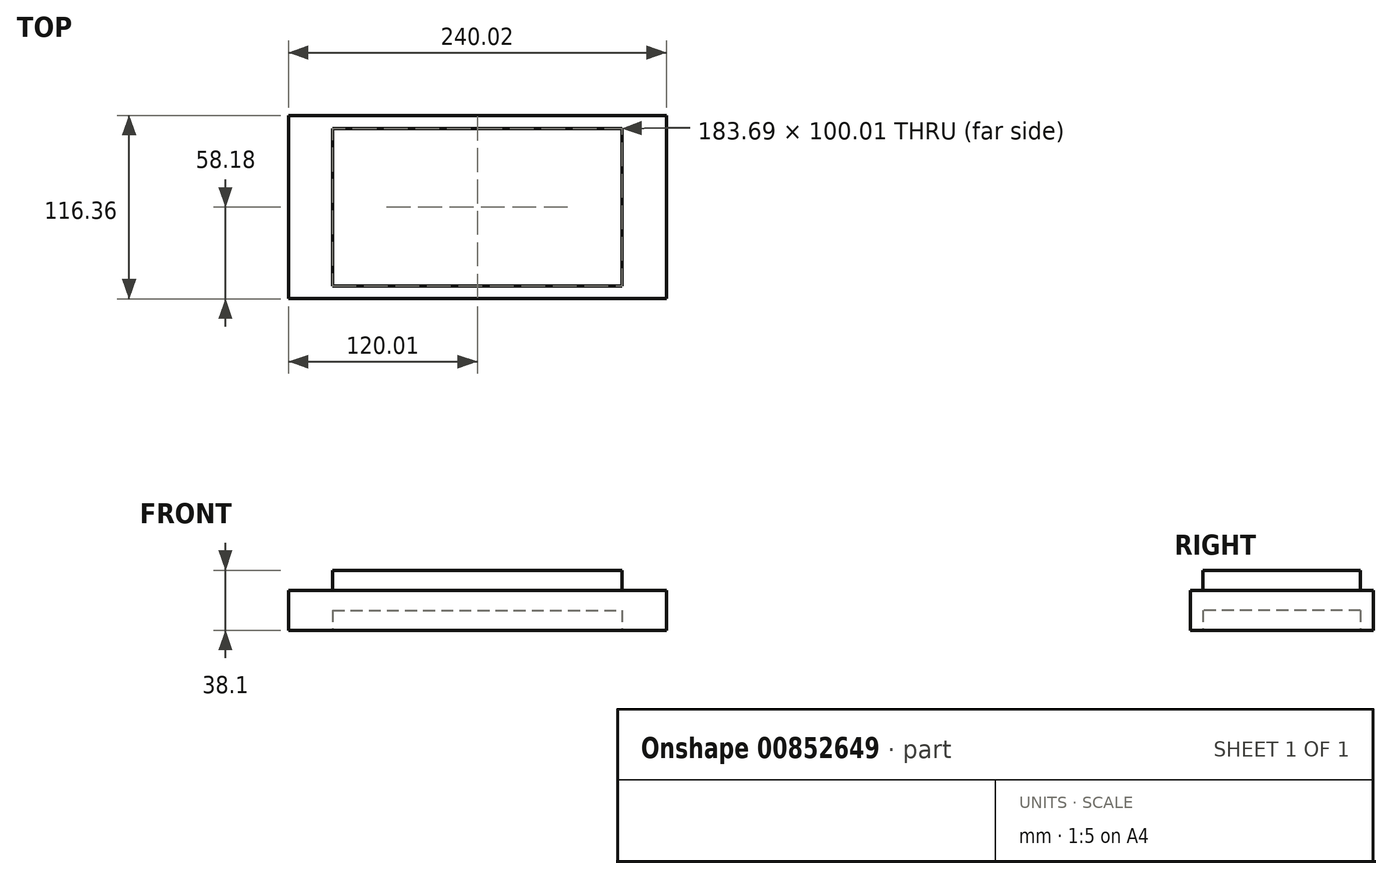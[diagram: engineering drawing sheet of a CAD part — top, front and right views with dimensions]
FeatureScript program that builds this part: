
annotation { "Feature Type Name" : "Feature", "Feature Type Description" : "" }
export const myFeature = defineFeature(function(context is Context, id is Id, definition is map)
    precondition{}
    {
        {
            var Q0;
            Q0=qCreatedBy(makeId("Top.planeOp"),FACE);
            var sketch = newSketch(context, id + "F0", { "sketchPlane" : qUnion([Q0])});
            skLineSegment(sketch, "E0.bottom", {"start": v(-91.84, 50) * mm, "end": v(91.84, 50) * mm});
            skLineSegment(sketch, "E0.top", {"start": v(-91.84, -50) * mm, "end": v(91.84, -50) * mm});
            skLineSegment(sketch, "E0.left", {"start": v(-91.84, 50) * mm, "end": v(-91.84, -50) * mm});
            skLineSegment(sketch, "E0.right", {"start": v(91.84, 50) * mm, "end": v(91.84, -50) * mm});
            skPoint(sketch, "E0.middle", {"position": v(0, 0) * mm});
            skLineSegment(sketch, "E1.bottom", {"start": v(-120.01, 58.18) * mm, "end": v(120.01, 58.18) * mm});
            skLineSegment(sketch, "E1.top", {"start": v(-120.01, -58.18) * mm, "end": v(120.01, -58.18) * mm});
            skLineSegment(sketch, "E1.left", {"start": v(-120.01, 58.18) * mm, "end": v(-120.01, -58.18) * mm});
            skLineSegment(sketch, "E1.right", {"start": v(120.01, 58.18) * mm, "end": v(120.01, -58.18) * mm});
            skSolve(sketch);
        }
        {
            var Q0;
            Q0=makeQuery(id+"F0.imprint","IMPRINT",FACE,{"disambiguationData":[TD([[makeQuery(id+"F0.imprint","IMPRINT",EDGE,{"derivedFrom":sQuery(id+"F0.wireOp",EDGE,"E0.bottom")}),-1.0]])]});
            extrude(context, id + "F1", {"entities" : qUnion([Q0]), "depth" : 25.4 * mm, "offsetDistance" : 25.4 * mm});
        }
        {
            var Q0;
            Q0 = qSketchRegion(id + "F0", true);
            extrude(context, id + "F2", {"entities" : qUnion([Q0]), "operationType" : NewBodyOperationType.ADD, "endBound" : BoundingType.SYMMETRIC, "depth" : 25.4 * mm, "offsetDistance" : 25.4 * mm});
        }
    });
